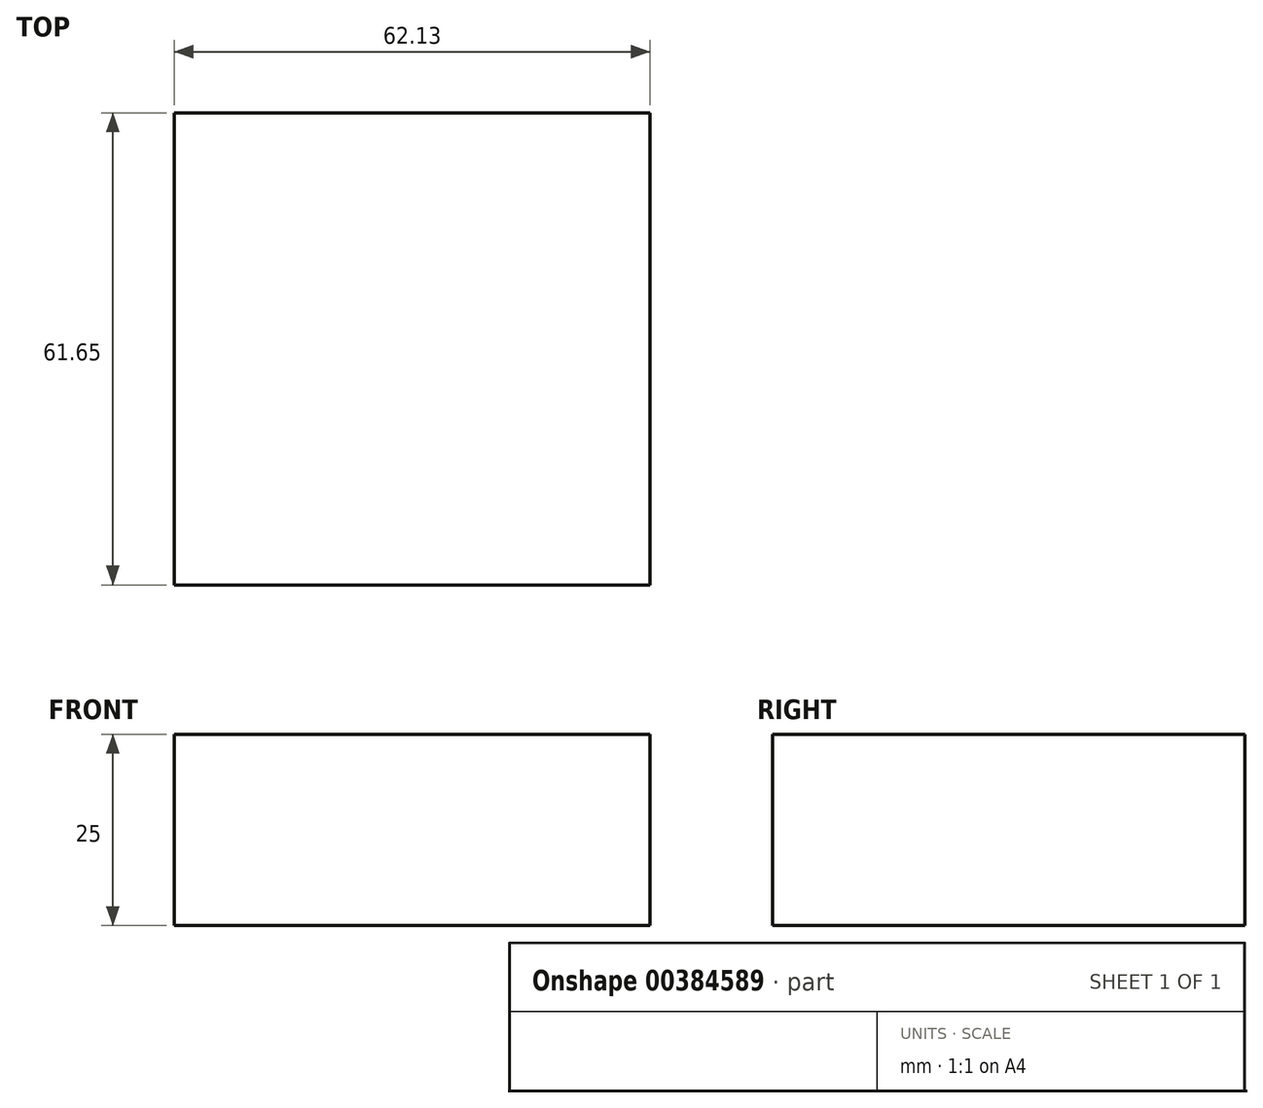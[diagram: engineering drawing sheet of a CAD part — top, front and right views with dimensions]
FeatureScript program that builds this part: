
annotation { "Feature Type Name" : "Feature", "Feature Type Description" : "" }
export const myFeature = defineFeature(function(context is Context, id is Id, definition is map)
    precondition{}
    {
        {
            var Q0;
            Q0=qCreatedBy(makeId("Top.planeOp"),FACE);
            var sketch = newSketch(context, id + "F0", { "sketchPlane" : qUnion([Q0])});
            skLineSegment(sketch, "E0", {"start": v(0, 0) * mm, "end": v(0, 61.65) * mm});
            skLineSegment(sketch, "E1", {"start": v(0, 61.65) * mm, "end": v(62.13, 61.65) * mm});
            skLineSegment(sketch, "E2", {"start": v(62.13, 61.65) * mm, "end": v(62.13, 0) * mm});
            skLineSegment(sketch, "E3", {"start": v(62.13, 0) * mm, "end": v(0, 0) * mm});
            skSolve(sketch);
        }
        {
            var Q0;
            Q0=makeQuery(id+"F0.imprint","IMPRINT",FACE,{"disambiguationData":[TD([[makeQuery(id+"F0.imprint","IMPRINT",EDGE,{"derivedFrom":sQuery(id+"F0.wireOp",EDGE,"E0")}),-1.0]])]});
            extrude(context, id + "F1", {"entities" : qUnion([Q0]), "depth" : 25 * mm});
        }
    });
